# Revit family: Haworth_Intuity_Parkbench_SeatingTable_EU_PRELIMINARY
name_source: partatom
category: Furniture
revit_build: Autodesk Revit 2018 (Build: 20170223_1515(x64)
units: mm (PartAtom-declared; Revit-internal decimal feet)

## family parameters
Always vertical = Yes
Cut with Voids When Loaded = No
OmniClass Number = 23.40.20.00
OmniClass Title = General Furniture and Specialties
Room Calculation Point = No
Shared = No
Work Plane-Based = No

## types (8) — shared parameters
Actual Height = 73 cm
Assembly Code = E2020200
Cord Height = 10 cm
Description = Haworth - Intuity - Parkbench - Seating Table
Glide Finish = Haworth _ Paint _ Allways Black
Manufacturer = Haworth
Max. Depth = 140 cm
Max. Width = 240 cm
Min. Depth = 100 cm
Min. Width = 160 cm
Model = PBSTXXXX
Size = Verify Final Dim. w/ Haworth
Tray Finish = Haworth _ Paint _ Allways White TROWC
URL = https://www.haworth.com
URL - Product = https://www.haworth.com
Version = 1
Warranty = http://www.haworth.com
With Top = Yes
with Cord = Yes

## per-type parameters (varying)
| type | Actual Depth | Actual Width | Casters | Depth | Glides | Glides Height | Tray Width | Width | Wood Offset |
| 2400 x 1400 | 140 cm | 240 cm | Yes | 140 cm | No | 9 cm | 150 cm | 240 cm | 60 cm |
| 2000 x 1400 | 140 cm | 200 cm | No | 140 cm | Yes | 2 cm | 110 cm | 200 cm | 50 cm |
| 2400 x 1200 | 120 cm | 240 cm | No | 120 cm | Yes | 2 cm | 150 cm | 240 cm | 60 cm |
| 2000 x 1200 | 120 cm | 200 cm | Yes | 120 cm | No | 9 cm | 110 cm | 200 cm | 50 cm |
| 2400 x 1000 | 100 cm | 240 cm | No | 100 cm | Yes | 2 cm | 150 cm | 240 cm | 60 cm |
| 2000 x 1000 | 100 cm | 200 cm | No | 100 cm | Yes | 2 cm | 110 cm | 200 cm | 50 cm |
| 1800 x 1000 | 100 cm | 180 cm | No | 100 cm | Yes | 2 cm | 90 cm | 180 cm | 45 cm |
| 1600 x 1000 | 100 cm | 160 cm | No | 100 cm | Yes | 2 cm | 70 cm | 160 cm | 40 cm |

## geometry (parser evidence)
native form markers: Sweep x10
no freeform markers — native parametric forms only
